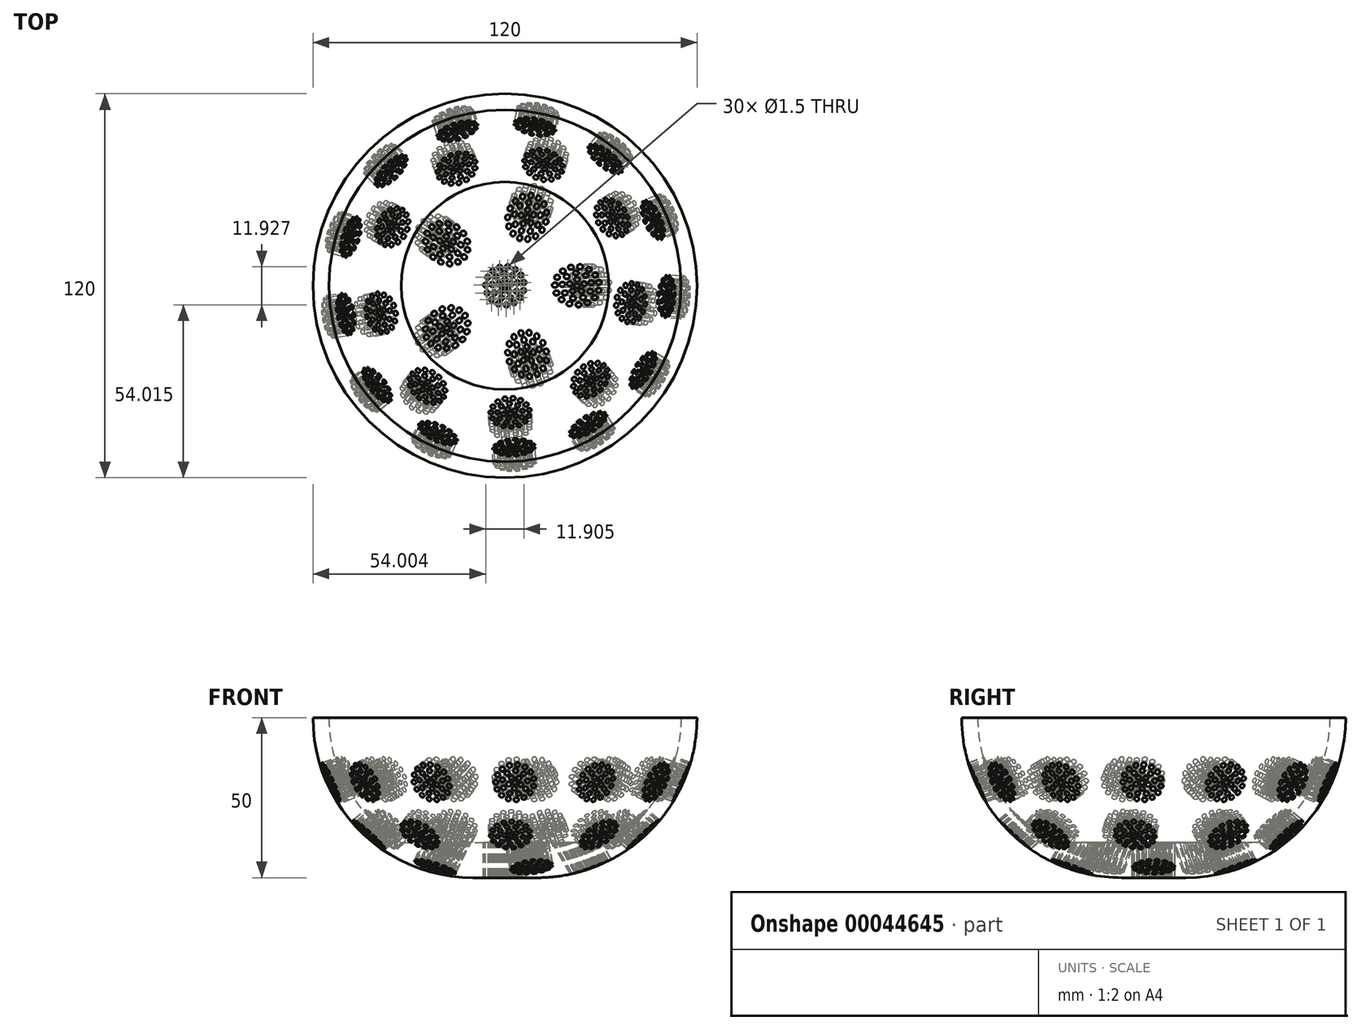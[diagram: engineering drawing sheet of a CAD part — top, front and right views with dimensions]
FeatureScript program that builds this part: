
annotation { "Feature Type Name" : "Feature", "Feature Type Description" : "" }
export const myFeature = defineFeature(function(context is Context, id is Id, definition is map)
    precondition{}
    {
        {
            var Q0;
            Q0=qCreatedBy(makeId("Front.planeOp"),FACE);
            var sketch = newSketch(context, id + "F0", { "sketchPlane" : qUnion([Q0])});
            skLineSegment(sketch, "E0", {"start": v(0, 0) * mm, "end": v(10, 0) * mm});
            skArc(sketch, "E1", {"start": v(10, 0) * mm, "mid": v(45.36, 14.64) * mm, "end": v(60, 50) * mm});
            skLineSegment(sketch, "E2", {"start": v(0, 0) * mm, "end": v(0, 50) * mm});
            skLineSegment(sketch, "E3", {"start": v(0, 50) * mm, "end": v(60, 50) * mm});
            skArc(sketch, "E4.0", {"start": v(32.45, 11) * mm, "mid": v(48.96, 27.47) * mm, "end": v(55, 50) * mm});
            skLineSegment(sketch, "E4.1", {"start": v(0, 11) * mm, "end": v(32.45, 11) * mm});
            skSolve(sketch);
        }
        {
            var Q0;
            {var subQ2=sQuery(id+"F0.wireOp",EDGE,"E0");Q0=makeQuery(id+"F0.imprint","IMPRINT",FACE,{"disambiguationData":[TD([[makeQuery(id+"F0.imprint","IMPRINT",EDGE,{"derivedFrom":subQ2}),1.0]])]});}
            var Q1;
            Q1=sQuery(id+"F0.wireOp",EDGE,"E2");
            revolve(context, id + "F1", {"entities" : qUnion([Q0]), "axis" : qUnion([Q1]), "revolveType" : RevolveType.FULL});
        }
        {
            var Q0;
            Q0=makeQuery(id+"F1.opRevolve","SWEPT_FACE",FACE,{"disambiguationData":[OSD([sQuery(id+"F0.wireOp",EDGE,"E4.1")])]});
            var sketch = newSketch(context, id + "F2", { "sketchPlane" : qUnion([Q0])});
            skCircle(sketch, "E5", {"center": v(0, 0) * mm, "radius": 0.75 * mm});
            skCircle(sketch, "E6", {"center": v(0, 2) * mm, "radius": 0.75 * mm});
            skCircle(sketch, "E7.1.0", {"center": v(-1.9, 0.62) * mm, "radius": 0.75 * mm});
            skCircle(sketch, "E7.2.0", {"center": v(-1.18, -1.62) * mm, "radius": 0.75 * mm});
            skCircle(sketch, "E7.3.0", {"center": v(1.18, -1.62) * mm, "radius": 0.75 * mm});
            skCircle(sketch, "E7.4.0", {"center": v(1.9, 0.62) * mm, "radius": 0.75 * mm});
            skLineSegment(sketch, "E8", {"start": v(0, 2) * mm, "end": v(1.9, 0.62) * mm, "construction": true});
            skLineSegment(sketch, "E9", {"start": v(0, 0) * mm, "end": v(0.95, 1.3) * mm, "construction": true});
            skLineSegment(sketch, "E10", {"start": v(0.95, 1.3) * mm, "end": v(2.35, 3.24) * mm, "construction": true});
            skCircle(sketch, "E11", {"center": v(2.35, 3.24) * mm, "radius": 0.75 * mm});
            skCircle(sketch, "E12.1.0", {"center": v(-0.28, 4) * mm, "radius": 0.75 * mm});
            skCircle(sketch, "E12.2.0", {"center": v(-2.78, 2.88) * mm, "radius": 0.75 * mm});
            skCircle(sketch, "E12.3.0", {"center": v(-3.98, 0.42) * mm, "radius": 0.75 * mm});
            skCircle(sketch, "E12.4.0", {"center": v(-3.32, -2.24) * mm, "radius": 0.75 * mm});
            skCircle(sketch, "E12.5.0", {"center": v(-1.1, -3.85) * mm, "radius": 0.75 * mm});
            skCircle(sketch, "E12.6.0", {"center": v(1.63, -3.65) * mm, "radius": 0.75 * mm});
            skCircle(sketch, "E13.1.7.0", {"center": v(3.6, -1.75) * mm, "radius": 0.75 * mm});
            skCircle(sketch, "E13.1.8.0", {"center": v(3.88, 0.97) * mm, "radius": 0.75 * mm});
            skLineSegment(sketch, "E14", {"start": v(3.88, 0.97) * mm, "end": v(2.35, 3.24) * mm, "construction": true});
            skLineSegment(sketch, "E15", {"start": v(0, 0) * mm, "end": v(3.12, 2.1) * mm, "construction": true});
            skLineSegment(sketch, "E16", {"start": v(3.12, 2.1) * mm, "end": v(4.97, 3.36) * mm, "construction": true});
            skCircle(sketch, "E17", {"center": v(4.97, 3.36) * mm, "radius": 0.75 * mm});
            skCircle(sketch, "E18.1.0", {"center": v(3.18, 5.09) * mm, "radius": 0.75 * mm});
            skCircle(sketch, "E18.2.0", {"center": v(0.84, 5.94) * mm, "radius": 0.75 * mm});
            skCircle(sketch, "E18.3.0", {"center": v(-1.65, 5.77) * mm, "radius": 0.75 * mm});
            skCircle(sketch, "E18.4.0", {"center": v(-3.86, 4.6) * mm, "radius": 0.75 * mm});
            skCircle(sketch, "E18.5.0", {"center": v(-5.4, 2.63) * mm, "radius": 0.75 * mm});
            skCircle(sketch, "E18.6.0", {"center": v(-6, 0.2) * mm, "radius": 0.75 * mm});
            skCircle(sketch, "E18.7.0", {"center": v(-5.56, -2.25) * mm, "radius": 0.75 * mm});
            skCircle(sketch, "E18.8.0", {"center": v(-4.17, -4.32) * mm, "radius": 0.75 * mm});
            skCircle(sketch, "E18.9.0", {"center": v(-2.05, -5.64) * mm, "radius": 0.75 * mm});
            skCircle(sketch, "E18.10.0", {"center": v(0.42, -5.99) * mm, "radius": 0.75 * mm});
            skCircle(sketch, "E18.11.0", {"center": v(2.82, -5.3) * mm, "radius": 0.75 * mm});
            skCircle(sketch, "E18.12.0", {"center": v(4.73, -3.7) * mm, "radius": 0.75 * mm});
            skCircle(sketch, "E18.13.0", {"center": v(5.82, -1.45) * mm, "radius": 0.75 * mm});
            skCircle(sketch, "E18.14.0", {"center": v(5.9, 1.04) * mm, "radius": 0.75 * mm});
            skSolve(sketch);
        }
        {
            var Q0;
            Q0=qSketchRegion(id+"F2",true);
            extrude(context, id + "F3", {"entities" : qUnion([Q0]), "operationType" : NewBodyOperationType.REMOVE, "oppositeDirection" : true, "depth" : 25 * mm});
        }
        {
            var Q0;
            Q0=makeQuery(id+"F1.opRevolve","SWEPT_FACE",FACE,{"disambiguationData":[OSD([sQuery(id+"F0.wireOp",EDGE,"E3")])]});
            var sketch = newSketch(context, id + "F4", { "sketchPlane" : qUnion([Q0])});
            skLineSegment(sketch, "E19", {"start": v(0, 55) * mm, "end": v(0, -55) * mm});
            skLineSegment(sketch, "E20", {"start": v(0, 0) * mm, "end": v(-29.42, 46.47) * mm});
            skLineSegment(sketch, "E21", {"start": v(0, 0) * mm, "end": v(-43.14, 34.11) * mm});
            skSolve(sketch);
        }
        {
            var Q0;
            Q0=makeQuery(id+"F3.boolean.opBoolean","COPY",FACE,{"derivedFrom":makeQuery(id+"F3.opExtrude","SWEPT_FACE",FACE,{"disambiguationData":[OSD([sQuery(id+"F2.wireOp",EDGE,"E18.7.0")])]})});
            var Q1;
            Q1=makeQuery(id+"F3.boolean.opBoolean","COPY",FACE,{"derivedFrom":makeQuery(id+"F3.opExtrude","SWEPT_FACE",FACE,{"disambiguationData":[OSD([sQuery(id+"F2.wireOp",EDGE,"E18.6.0")])]})});
            var Q2;
            Q2=makeQuery(id+"F3.boolean.opBoolean","COPY",FACE,{"derivedFrom":makeQuery(id+"F3.opExtrude","SWEPT_FACE",FACE,{"disambiguationData":[OSD([sQuery(id+"F2.wireOp",EDGE,"E18.5.0")])]})});
            var Q3;
            Q3=makeQuery(id+"F3.boolean.opBoolean","COPY",FACE,{"derivedFrom":makeQuery(id+"F3.opExtrude","SWEPT_FACE",FACE,{"disambiguationData":[OSD([sQuery(id+"F2.wireOp",EDGE,"E18.4.0")])]})});
            var Q4;
            Q4=makeQuery(id+"F3.boolean.opBoolean","COPY",FACE,{"derivedFrom":makeQuery(id+"F3.opExtrude","SWEPT_FACE",FACE,{"disambiguationData":[OSD([sQuery(id+"F2.wireOp",EDGE,"E18.3.0")])]})});
            var Q5;
            Q5=makeQuery(id+"F3.boolean.opBoolean","COPY",FACE,{"derivedFrom":makeQuery(id+"F3.opExtrude","SWEPT_FACE",FACE,{"disambiguationData":[OSD([sQuery(id+"F2.wireOp",EDGE,"E18.2.0")])]})});
            var Q6;
            Q6=makeQuery(id+"F3.boolean.opBoolean","COPY",FACE,{"derivedFrom":makeQuery(id+"F3.opExtrude","SWEPT_FACE",FACE,{"disambiguationData":[OSD([sQuery(id+"F2.wireOp",EDGE,"E18.1.0")])]})});
            var Q7;
            Q7=makeQuery(id+"F3.boolean.opBoolean","COPY",FACE,{"derivedFrom":makeQuery(id+"F3.opExtrude","SWEPT_FACE",FACE,{"disambiguationData":[OSD([sQuery(id+"F2.wireOp",EDGE,"E17")])]})});
            var Q8;
            Q8=makeQuery(id+"F3.boolean.opBoolean","COPY",FACE,{"derivedFrom":makeQuery(id+"F3.opExtrude","SWEPT_FACE",FACE,{"disambiguationData":[OSD([sQuery(id+"F2.wireOp",EDGE,"E18.14.0")])]})});
            var Q9;
            Q9=makeQuery(id+"F3.boolean.opBoolean","COPY",FACE,{"derivedFrom":makeQuery(id+"F3.opExtrude","SWEPT_FACE",FACE,{"disambiguationData":[OSD([sQuery(id+"F2.wireOp",EDGE,"E18.13.0")])]})});
            var Q10;
            Q10=makeQuery(id+"F3.boolean.opBoolean","COPY",FACE,{"derivedFrom":makeQuery(id+"F3.opExtrude","SWEPT_FACE",FACE,{"disambiguationData":[OSD([sQuery(id+"F2.wireOp",EDGE,"E18.12.0")])]})});
            var Q11;
            Q11=makeQuery(id+"F3.boolean.opBoolean","COPY",FACE,{"derivedFrom":makeQuery(id+"F3.opExtrude","SWEPT_FACE",FACE,{"disambiguationData":[OSD([sQuery(id+"F2.wireOp",EDGE,"E18.11.0")])]})});
            var Q12;
            Q12=makeQuery(id+"F3.boolean.opBoolean","COPY",FACE,{"derivedFrom":makeQuery(id+"F3.opExtrude","SWEPT_FACE",FACE,{"disambiguationData":[OSD([sQuery(id+"F2.wireOp",EDGE,"E18.10.0")])]})});
            var Q13;
            Q13=makeQuery(id+"F3.boolean.opBoolean","COPY",FACE,{"derivedFrom":makeQuery(id+"F3.opExtrude","SWEPT_FACE",FACE,{"disambiguationData":[OSD([sQuery(id+"F2.wireOp",EDGE,"E18.9.0")])]})});
            var Q14;
            Q14=makeQuery(id+"F3.boolean.opBoolean","COPY",FACE,{"derivedFrom":makeQuery(id+"F3.opExtrude","SWEPT_FACE",FACE,{"disambiguationData":[OSD([sQuery(id+"F2.wireOp",EDGE,"E18.8.0")])]})});
            var Q15;
            Q15=makeQuery(id+"F3.boolean.opBoolean","COPY",FACE,{"derivedFrom":makeQuery(id+"F3.opExtrude","SWEPT_FACE",FACE,{"disambiguationData":[OSD([sQuery(id+"F2.wireOp",EDGE,"E12.4.0")])]})});
            var Q16;
            Q16=makeQuery(id+"F3.boolean.opBoolean","COPY",FACE,{"derivedFrom":makeQuery(id+"F3.opExtrude","SWEPT_FACE",FACE,{"disambiguationData":[OSD([sQuery(id+"F2.wireOp",EDGE,"E12.3.0")])]})});
            var Q17;
            Q17=makeQuery(id+"F3.boolean.opBoolean","COPY",FACE,{"derivedFrom":makeQuery(id+"F3.opExtrude","SWEPT_FACE",FACE,{"disambiguationData":[OSD([sQuery(id+"F2.wireOp",EDGE,"E12.2.0")])]})});
            var Q18;
            Q18=makeQuery(id+"F3.boolean.opBoolean","COPY",FACE,{"derivedFrom":makeQuery(id+"F3.opExtrude","SWEPT_FACE",FACE,{"disambiguationData":[OSD([sQuery(id+"F2.wireOp",EDGE,"E12.1.0")])]})});
            var Q19;
            Q19=makeQuery(id+"F3.boolean.opBoolean","COPY",FACE,{"derivedFrom":makeQuery(id+"F3.opExtrude","SWEPT_FACE",FACE,{"disambiguationData":[OSD([sQuery(id+"F2.wireOp",EDGE,"E11")])]})});
            var Q20;
            Q20=makeQuery(id+"F3.boolean.opBoolean","COPY",FACE,{"derivedFrom":makeQuery(id+"F3.opExtrude","SWEPT_FACE",FACE,{"disambiguationData":[OSD([sQuery(id+"F2.wireOp",EDGE,"E13.1.8.0")])]})});
            var Q21;
            Q21=makeQuery(id+"F3.boolean.opBoolean","COPY",FACE,{"derivedFrom":makeQuery(id+"F3.opExtrude","SWEPT_FACE",FACE,{"disambiguationData":[OSD([sQuery(id+"F2.wireOp",EDGE,"E13.1.7.0")])]})});
            var Q22;
            Q22=makeQuery(id+"F3.boolean.opBoolean","COPY",FACE,{"derivedFrom":makeQuery(id+"F3.opExtrude","SWEPT_FACE",FACE,{"disambiguationData":[OSD([sQuery(id+"F2.wireOp",EDGE,"E12.6.0")])]})});
            var Q23;
            Q23=makeQuery(id+"F3.boolean.opBoolean","COPY",FACE,{"derivedFrom":makeQuery(id+"F3.opExtrude","SWEPT_FACE",FACE,{"disambiguationData":[OSD([sQuery(id+"F2.wireOp",EDGE,"E12.5.0")])]})});
            var Q24;
            Q24=makeQuery(id+"F3.boolean.opBoolean","COPY",FACE,{"derivedFrom":makeQuery(id+"F3.opExtrude","SWEPT_FACE",FACE,{"disambiguationData":[OSD([sQuery(id+"F2.wireOp",EDGE,"E7.2.0")])]})});
            var Q25;
            Q25=makeQuery(id+"F3.boolean.opBoolean","COPY",FACE,{"derivedFrom":makeQuery(id+"F3.opExtrude","SWEPT_FACE",FACE,{"disambiguationData":[OSD([sQuery(id+"F2.wireOp",EDGE,"E7.1.0")])]})});
            var Q26;
            Q26=makeQuery(id+"F3.boolean.opBoolean","COPY",FACE,{"derivedFrom":makeQuery(id+"F3.opExtrude","SWEPT_FACE",FACE,{"disambiguationData":[OSD([sQuery(id+"F2.wireOp",EDGE,"E6")])]})});
            var Q27;
            Q27=makeQuery(id+"F3.boolean.opBoolean","COPY",FACE,{"derivedFrom":makeQuery(id+"F3.opExtrude","SWEPT_FACE",FACE,{"disambiguationData":[OSD([sQuery(id+"F2.wireOp",EDGE,"E7.4.0")])]})});
            var Q28;
            Q28=makeQuery(id+"F3.boolean.opBoolean","COPY",FACE,{"derivedFrom":makeQuery(id+"F3.opExtrude","SWEPT_FACE",FACE,{"disambiguationData":[OSD([sQuery(id+"F2.wireOp",EDGE,"E7.3.0")])]})});
            var Q29;
            Q29=makeQuery(id+"F3.boolean.opBoolean","COPY",FACE,{"derivedFrom":makeQuery(id+"F3.opExtrude","SWEPT_FACE",FACE,{"disambiguationData":[OSD([sQuery(id+"F2.wireOp",EDGE,"E5")])]})});
            var Q30;
            Q30=sQuery(id+"F4.wireOp",EDGE,"E19");
            circularPattern(context, id + "F5", {"faces" : qUnion([Q0, Q1, Q2, Q3, Q4, Q5, Q6, Q7, Q8, Q9, Q10, Q11, Q12, Q13, Q14, Q15, Q16, Q17, Q18, Q19, Q20, Q21, Q22, Q23, Q24, Q25, Q26, Q27, Q28, Q29]), "axis" : qUnion([Q30]), "angle" : 30 * degree, "instanceCount" : 2, "patternType" : PatternType.FACE});
        }
        {
            var Q0;
            Q0=makeQuery(id+"F5.opPattern","COPY",FACE,{"derivedFrom":makeQuery(id+"F3.boolean.opBoolean","COPY",FACE,{"derivedFrom":makeQuery(id+"F3.opExtrude","SWEPT_FACE",FACE,{"disambiguationData":[OSD([sQuery(id+"F2.wireOp",EDGE,"E18.5.0")])]})}),"instanceName":"1"});
            var Q1;
            Q1=makeQuery(id+"F5.opPattern","COPY",FACE,{"derivedFrom":makeQuery(id+"F3.boolean.opBoolean","COPY",FACE,{"derivedFrom":makeQuery(id+"F3.opExtrude","SWEPT_FACE",FACE,{"disambiguationData":[OSD([sQuery(id+"F2.wireOp",EDGE,"E18.6.0")])]})}),"instanceName":"1"});
            var Q2;
            Q2=makeQuery(id+"F5.opPattern","COPY",FACE,{"derivedFrom":makeQuery(id+"F3.boolean.opBoolean","COPY",FACE,{"derivedFrom":makeQuery(id+"F3.opExtrude","SWEPT_FACE",FACE,{"disambiguationData":[OSD([sQuery(id+"F2.wireOp",EDGE,"E18.7.0")])]})}),"instanceName":"1"});
            var Q3;
            Q3=makeQuery(id+"F5.opPattern","COPY",FACE,{"derivedFrom":makeQuery(id+"F3.boolean.opBoolean","COPY",FACE,{"derivedFrom":makeQuery(id+"F3.opExtrude","SWEPT_FACE",FACE,{"disambiguationData":[OSD([sQuery(id+"F2.wireOp",EDGE,"E18.8.0")])]})}),"instanceName":"1"});
            var Q4;
            Q4=makeQuery(id+"F5.opPattern","COPY",FACE,{"derivedFrom":makeQuery(id+"F3.boolean.opBoolean","COPY",FACE,{"derivedFrom":makeQuery(id+"F3.opExtrude","SWEPT_FACE",FACE,{"disambiguationData":[OSD([sQuery(id+"F2.wireOp",EDGE,"E18.9.0")])]})}),"instanceName":"1"});
            var Q5;
            Q5=makeQuery(id+"F5.opPattern","COPY",FACE,{"derivedFrom":makeQuery(id+"F3.boolean.opBoolean","COPY",FACE,{"derivedFrom":makeQuery(id+"F3.opExtrude","SWEPT_FACE",FACE,{"disambiguationData":[OSD([sQuery(id+"F2.wireOp",EDGE,"E18.11.0")])]})}),"instanceName":"1"});
            var Q6;
            Q6=makeQuery(id+"F5.opPattern","COPY",FACE,{"derivedFrom":makeQuery(id+"F3.boolean.opBoolean","COPY",FACE,{"derivedFrom":makeQuery(id+"F3.opExtrude","SWEPT_FACE",FACE,{"disambiguationData":[OSD([sQuery(id+"F2.wireOp",EDGE,"E18.12.0")])]})}),"instanceName":"1"});
            var Q7;
            Q7=makeQuery(id+"F5.opPattern","COPY",FACE,{"derivedFrom":makeQuery(id+"F3.boolean.opBoolean","COPY",FACE,{"derivedFrom":makeQuery(id+"F3.opExtrude","SWEPT_FACE",FACE,{"disambiguationData":[OSD([sQuery(id+"F2.wireOp",EDGE,"E18.13.0")])]})}),"instanceName":"1"});
            var Q8;
            Q8=makeQuery(id+"F5.opPattern","COPY",FACE,{"derivedFrom":makeQuery(id+"F3.boolean.opBoolean","COPY",FACE,{"derivedFrom":makeQuery(id+"F3.opExtrude","SWEPT_FACE",FACE,{"disambiguationData":[OSD([sQuery(id+"F2.wireOp",EDGE,"E18.14.0")])]})}),"instanceName":"1"});
            var Q9;
            Q9=makeQuery(id+"F5.opPattern","COPY",FACE,{"derivedFrom":makeQuery(id+"F3.boolean.opBoolean","COPY",FACE,{"derivedFrom":makeQuery(id+"F3.opExtrude","SWEPT_FACE",FACE,{"disambiguationData":[OSD([sQuery(id+"F2.wireOp",EDGE,"E17")])]})}),"instanceName":"1"});
            var Q10;
            Q10=makeQuery(id+"F5.opPattern","COPY",FACE,{"derivedFrom":makeQuery(id+"F3.boolean.opBoolean","COPY",FACE,{"derivedFrom":makeQuery(id+"F3.opExtrude","SWEPT_FACE",FACE,{"disambiguationData":[OSD([sQuery(id+"F2.wireOp",EDGE,"E18.1.0")])]})}),"instanceName":"1"});
            var Q11;
            Q11=makeQuery(id+"F5.opPattern","COPY",FACE,{"derivedFrom":makeQuery(id+"F3.boolean.opBoolean","COPY",FACE,{"derivedFrom":makeQuery(id+"F3.opExtrude","SWEPT_FACE",FACE,{"disambiguationData":[OSD([sQuery(id+"F2.wireOp",EDGE,"E18.2.0")])]})}),"instanceName":"1"});
            var Q12;
            Q12=makeQuery(id+"F5.opPattern","COPY",FACE,{"derivedFrom":makeQuery(id+"F3.boolean.opBoolean","COPY",FACE,{"derivedFrom":makeQuery(id+"F3.opExtrude","SWEPT_FACE",FACE,{"disambiguationData":[OSD([sQuery(id+"F2.wireOp",EDGE,"E18.3.0")])]})}),"instanceName":"1"});
            var Q13;
            Q13=makeQuery(id+"F5.opPattern","COPY",FACE,{"derivedFrom":makeQuery(id+"F3.boolean.opBoolean","COPY",FACE,{"derivedFrom":makeQuery(id+"F3.opExtrude","SWEPT_FACE",FACE,{"disambiguationData":[OSD([sQuery(id+"F2.wireOp",EDGE,"E18.4.0")])]})}),"instanceName":"1"});
            var Q14;
            Q14=makeQuery(id+"F5.opPattern","COPY",FACE,{"derivedFrom":makeQuery(id+"F3.boolean.opBoolean","COPY",FACE,{"derivedFrom":makeQuery(id+"F3.opExtrude","SWEPT_FACE",FACE,{"disambiguationData":[OSD([sQuery(id+"F2.wireOp",EDGE,"E12.2.0")])]})}),"instanceName":"1"});
            var Q15;
            Q15=makeQuery(id+"F5.opPattern","COPY",FACE,{"derivedFrom":makeQuery(id+"F3.boolean.opBoolean","COPY",FACE,{"derivedFrom":makeQuery(id+"F3.opExtrude","SWEPT_FACE",FACE,{"disambiguationData":[OSD([sQuery(id+"F2.wireOp",EDGE,"E12.3.0")])]})}),"instanceName":"1"});
            var Q16;
            Q16=makeQuery(id+"F5.opPattern","COPY",FACE,{"derivedFrom":makeQuery(id+"F3.boolean.opBoolean","COPY",FACE,{"derivedFrom":makeQuery(id+"F3.opExtrude","SWEPT_FACE",FACE,{"disambiguationData":[OSD([sQuery(id+"F2.wireOp",EDGE,"E12.4.0")])]})}),"instanceName":"1"});
            var Q17;
            Q17=makeQuery(id+"F5.opPattern","COPY",FACE,{"derivedFrom":makeQuery(id+"F3.boolean.opBoolean","COPY",FACE,{"derivedFrom":makeQuery(id+"F3.opExtrude","SWEPT_FACE",FACE,{"disambiguationData":[OSD([sQuery(id+"F2.wireOp",EDGE,"E12.6.0")])]})}),"instanceName":"1"});
            var Q18;
            Q18=makeQuery(id+"F5.opPattern","COPY",FACE,{"derivedFrom":makeQuery(id+"F3.boolean.opBoolean","COPY",FACE,{"derivedFrom":makeQuery(id+"F3.opExtrude","SWEPT_FACE",FACE,{"disambiguationData":[OSD([sQuery(id+"F2.wireOp",EDGE,"E13.1.7.0")])]})}),"instanceName":"1"});
            var Q19;
            Q19=makeQuery(id+"F5.opPattern","COPY",FACE,{"derivedFrom":makeQuery(id+"F3.boolean.opBoolean","COPY",FACE,{"derivedFrom":makeQuery(id+"F3.opExtrude","SWEPT_FACE",FACE,{"disambiguationData":[OSD([sQuery(id+"F2.wireOp",EDGE,"E18.10.0")])]})}),"instanceName":"1"});
            var Q20;
            Q20=makeQuery(id+"F5.opPattern","COPY",FACE,{"derivedFrom":makeQuery(id+"F3.boolean.opBoolean","COPY",FACE,{"derivedFrom":makeQuery(id+"F3.opExtrude","SWEPT_FACE",FACE,{"disambiguationData":[OSD([sQuery(id+"F2.wireOp",EDGE,"E12.5.0")])]})}),"instanceName":"1"});
            var Q21;
            Q21=makeQuery(id+"F5.opPattern","COPY",FACE,{"derivedFrom":makeQuery(id+"F3.boolean.opBoolean","COPY",FACE,{"derivedFrom":makeQuery(id+"F3.opExtrude","SWEPT_FACE",FACE,{"disambiguationData":[OSD([sQuery(id+"F2.wireOp",EDGE,"E7.2.0")])]})}),"instanceName":"1"});
            var Q22;
            Q22=makeQuery(id+"F5.opPattern","COPY",FACE,{"derivedFrom":makeQuery(id+"F3.boolean.opBoolean","COPY",FACE,{"derivedFrom":makeQuery(id+"F3.opExtrude","SWEPT_FACE",FACE,{"disambiguationData":[OSD([sQuery(id+"F2.wireOp",EDGE,"E5")])]})}),"instanceName":"1"});
            var Q23;
            Q23=makeQuery(id+"F5.opPattern","COPY",FACE,{"derivedFrom":makeQuery(id+"F3.boolean.opBoolean","COPY",FACE,{"derivedFrom":makeQuery(id+"F3.opExtrude","SWEPT_FACE",FACE,{"disambiguationData":[OSD([sQuery(id+"F2.wireOp",EDGE,"E6")])]})}),"instanceName":"1"});
            var Q24;
            Q24=makeQuery(id+"F5.opPattern","COPY",FACE,{"derivedFrom":makeQuery(id+"F3.boolean.opBoolean","COPY",FACE,{"derivedFrom":makeQuery(id+"F3.opExtrude","SWEPT_FACE",FACE,{"disambiguationData":[OSD([sQuery(id+"F2.wireOp",EDGE,"E7.4.0")])]})}),"instanceName":"1"});
            var Q25;
            Q25=makeQuery(id+"F5.opPattern","COPY",FACE,{"derivedFrom":makeQuery(id+"F3.boolean.opBoolean","COPY",FACE,{"derivedFrom":makeQuery(id+"F3.opExtrude","SWEPT_FACE",FACE,{"disambiguationData":[OSD([sQuery(id+"F2.wireOp",EDGE,"E7.3.0")])]})}),"instanceName":"1"});
            var Q26;
            Q26=makeQuery(id+"F5.opPattern","COPY",FACE,{"derivedFrom":makeQuery(id+"F3.boolean.opBoolean","COPY",FACE,{"derivedFrom":makeQuery(id+"F3.opExtrude","SWEPT_FACE",FACE,{"disambiguationData":[OSD([sQuery(id+"F2.wireOp",EDGE,"E13.1.8.0")])]})}),"instanceName":"1"});
            var Q27;
            Q27=makeQuery(id+"F5.opPattern","COPY",FACE,{"derivedFrom":makeQuery(id+"F3.boolean.opBoolean","COPY",FACE,{"derivedFrom":makeQuery(id+"F3.opExtrude","SWEPT_FACE",FACE,{"disambiguationData":[OSD([sQuery(id+"F2.wireOp",EDGE,"E11")])]})}),"instanceName":"1"});
            var Q28;
            Q28=makeQuery(id+"F5.opPattern","COPY",FACE,{"derivedFrom":makeQuery(id+"F3.boolean.opBoolean","COPY",FACE,{"derivedFrom":makeQuery(id+"F3.opExtrude","SWEPT_FACE",FACE,{"disambiguationData":[OSD([sQuery(id+"F2.wireOp",EDGE,"E12.1.0")])]})}),"instanceName":"1"});
            var Q29;
            Q29=makeQuery(id+"F5.opPattern","COPY",FACE,{"derivedFrom":makeQuery(id+"F3.boolean.opBoolean","COPY",FACE,{"derivedFrom":makeQuery(id+"F3.opExtrude","SWEPT_FACE",FACE,{"disambiguationData":[OSD([sQuery(id+"F2.wireOp",EDGE,"E7.1.0")])]})}),"instanceName":"1"});
            var Q30;
            Q30=sQuery(id+"F0.wireOp",EDGE,"E2");
            circularPattern(context, id + "F6", {"faces" : qUnion([Q0, Q1, Q2, Q3, Q4, Q5, Q6, Q7, Q8, Q9, Q10, Q11, Q12, Q13, Q14, Q15, Q16, Q17, Q18, Q19, Q20, Q21, Q22, Q23, Q24, Q25, Q26, Q27, Q28, Q29]), "axis" : qUnion([Q30]), "angle" : 360 * degree, "instanceCount" : round(5), "equalSpace" : true, "patternType" : PatternType.FACE});
        }
        {
            var Q0;
            Q0=makeQuery(id+"F3.boolean.opBoolean","COPY",FACE,{"derivedFrom":makeQuery(id+"F3.opExtrude","SWEPT_FACE",FACE,{"disambiguationData":[OSD([sQuery(id+"F2.wireOp",EDGE,"E18.1.0")])]})});
            var Q1;
            Q1=makeQuery(id+"F3.boolean.opBoolean","COPY",FACE,{"derivedFrom":makeQuery(id+"F3.opExtrude","SWEPT_FACE",FACE,{"disambiguationData":[OSD([sQuery(id+"F2.wireOp",EDGE,"E18.2.0")])]})});
            var Q2;
            Q2=makeQuery(id+"F3.boolean.opBoolean","COPY",FACE,{"derivedFrom":makeQuery(id+"F3.opExtrude","SWEPT_FACE",FACE,{"disambiguationData":[OSD([sQuery(id+"F2.wireOp",EDGE,"E18.3.0")])]})});
            var Q3;
            Q3=makeQuery(id+"F3.boolean.opBoolean","COPY",FACE,{"derivedFrom":makeQuery(id+"F3.opExtrude","SWEPT_FACE",FACE,{"disambiguationData":[OSD([sQuery(id+"F2.wireOp",EDGE,"E18.4.0")])]})});
            var Q4;
            Q4=makeQuery(id+"F3.boolean.opBoolean","COPY",FACE,{"derivedFrom":makeQuery(id+"F3.opExtrude","SWEPT_FACE",FACE,{"disambiguationData":[OSD([sQuery(id+"F2.wireOp",EDGE,"E18.5.0")])]})});
            var Q5;
            Q5=makeQuery(id+"F3.boolean.opBoolean","COPY",FACE,{"derivedFrom":makeQuery(id+"F3.opExtrude","SWEPT_FACE",FACE,{"disambiguationData":[OSD([sQuery(id+"F2.wireOp",EDGE,"E18.6.0")])]})});
            var Q6;
            Q6=makeQuery(id+"F3.boolean.opBoolean","COPY",FACE,{"derivedFrom":makeQuery(id+"F3.opExtrude","SWEPT_FACE",FACE,{"disambiguationData":[OSD([sQuery(id+"F2.wireOp",EDGE,"E18.7.0")])]})});
            var Q7;
            Q7=makeQuery(id+"F3.boolean.opBoolean","COPY",FACE,{"derivedFrom":makeQuery(id+"F3.opExtrude","SWEPT_FACE",FACE,{"disambiguationData":[OSD([sQuery(id+"F2.wireOp",EDGE,"E18.8.0")])]})});
            var Q8;
            Q8=makeQuery(id+"F3.boolean.opBoolean","COPY",FACE,{"derivedFrom":makeQuery(id+"F3.opExtrude","SWEPT_FACE",FACE,{"disambiguationData":[OSD([sQuery(id+"F2.wireOp",EDGE,"E18.9.0")])]})});
            var Q9;
            Q9=makeQuery(id+"F3.boolean.opBoolean","COPY",FACE,{"derivedFrom":makeQuery(id+"F3.opExtrude","SWEPT_FACE",FACE,{"disambiguationData":[OSD([sQuery(id+"F2.wireOp",EDGE,"E18.10.0")])]})});
            var Q10;
            Q10=makeQuery(id+"F3.boolean.opBoolean","COPY",FACE,{"derivedFrom":makeQuery(id+"F3.opExtrude","SWEPT_FACE",FACE,{"disambiguationData":[OSD([sQuery(id+"F2.wireOp",EDGE,"E18.11.0")])]})});
            var Q11;
            Q11=makeQuery(id+"F3.boolean.opBoolean","COPY",FACE,{"derivedFrom":makeQuery(id+"F3.opExtrude","SWEPT_FACE",FACE,{"disambiguationData":[OSD([sQuery(id+"F2.wireOp",EDGE,"E18.12.0")])]})});
            var Q12;
            Q12=makeQuery(id+"F3.boolean.opBoolean","COPY",FACE,{"derivedFrom":makeQuery(id+"F3.opExtrude","SWEPT_FACE",FACE,{"disambiguationData":[OSD([sQuery(id+"F2.wireOp",EDGE,"E18.13.0")])]})});
            var Q13;
            Q13=makeQuery(id+"F3.boolean.opBoolean","COPY",FACE,{"derivedFrom":makeQuery(id+"F3.opExtrude","SWEPT_FACE",FACE,{"disambiguationData":[OSD([sQuery(id+"F2.wireOp",EDGE,"E18.14.0")])]})});
            var Q14;
            Q14=makeQuery(id+"F3.boolean.opBoolean","COPY",FACE,{"derivedFrom":makeQuery(id+"F3.opExtrude","SWEPT_FACE",FACE,{"disambiguationData":[OSD([sQuery(id+"F2.wireOp",EDGE,"E13.1.8.0")])]})});
            var Q15;
            Q15=makeQuery(id+"F3.boolean.opBoolean","COPY",FACE,{"derivedFrom":makeQuery(id+"F3.opExtrude","SWEPT_FACE",FACE,{"disambiguationData":[OSD([sQuery(id+"F2.wireOp",EDGE,"E11")])]})});
            var Q16;
            Q16=makeQuery(id+"F3.boolean.opBoolean","COPY",FACE,{"derivedFrom":makeQuery(id+"F3.opExtrude","SWEPT_FACE",FACE,{"disambiguationData":[OSD([sQuery(id+"F2.wireOp",EDGE,"E12.1.0")])]})});
            var Q17;
            Q17=makeQuery(id+"F3.boolean.opBoolean","COPY",FACE,{"derivedFrom":makeQuery(id+"F3.opExtrude","SWEPT_FACE",FACE,{"disambiguationData":[OSD([sQuery(id+"F2.wireOp",EDGE,"E12.2.0")])]})});
            var Q18;
            Q18=makeQuery(id+"F3.boolean.opBoolean","COPY",FACE,{"derivedFrom":makeQuery(id+"F3.opExtrude","SWEPT_FACE",FACE,{"disambiguationData":[OSD([sQuery(id+"F2.wireOp",EDGE,"E12.3.0")])]})});
            var Q19;
            Q19=makeQuery(id+"F3.boolean.opBoolean","COPY",FACE,{"derivedFrom":makeQuery(id+"F3.opExtrude","SWEPT_FACE",FACE,{"disambiguationData":[OSD([sQuery(id+"F2.wireOp",EDGE,"E12.4.0")])]})});
            var Q20;
            Q20=makeQuery(id+"F3.boolean.opBoolean","COPY",FACE,{"derivedFrom":makeQuery(id+"F3.opExtrude","SWEPT_FACE",FACE,{"disambiguationData":[OSD([sQuery(id+"F2.wireOp",EDGE,"E12.5.0")])]})});
            var Q21;
            Q21=makeQuery(id+"F3.boolean.opBoolean","COPY",FACE,{"derivedFrom":makeQuery(id+"F3.opExtrude","SWEPT_FACE",FACE,{"disambiguationData":[OSD([sQuery(id+"F2.wireOp",EDGE,"E12.6.0")])]})});
            var Q22;
            Q22=makeQuery(id+"F3.boolean.opBoolean","COPY",FACE,{"derivedFrom":makeQuery(id+"F3.opExtrude","SWEPT_FACE",FACE,{"disambiguationData":[OSD([sQuery(id+"F2.wireOp",EDGE,"E13.1.7.0")])]})});
            var Q23;
            Q23=makeQuery(id+"F3.boolean.opBoolean","COPY",FACE,{"derivedFrom":makeQuery(id+"F3.opExtrude","SWEPT_FACE",FACE,{"disambiguationData":[OSD([sQuery(id+"F2.wireOp",EDGE,"E7.4.0")])]})});
            var Q24;
            Q24=makeQuery(id+"F3.boolean.opBoolean","COPY",FACE,{"derivedFrom":makeQuery(id+"F3.opExtrude","SWEPT_FACE",FACE,{"disambiguationData":[OSD([sQuery(id+"F2.wireOp",EDGE,"E6")])]})});
            var Q25;
            Q25=makeQuery(id+"F3.boolean.opBoolean","COPY",FACE,{"derivedFrom":makeQuery(id+"F3.opExtrude","SWEPT_FACE",FACE,{"disambiguationData":[OSD([sQuery(id+"F2.wireOp",EDGE,"E7.1.0")])]})});
            var Q26;
            Q26=makeQuery(id+"F3.boolean.opBoolean","COPY",FACE,{"derivedFrom":makeQuery(id+"F3.opExtrude","SWEPT_FACE",FACE,{"disambiguationData":[OSD([sQuery(id+"F2.wireOp",EDGE,"E7.2.0")])]})});
            var Q27;
            Q27=makeQuery(id+"F3.boolean.opBoolean","COPY",FACE,{"derivedFrom":makeQuery(id+"F3.opExtrude","SWEPT_FACE",FACE,{"disambiguationData":[OSD([sQuery(id+"F2.wireOp",EDGE,"E5")])]})});
            var Q28;
            Q28=makeQuery(id+"F3.boolean.opBoolean","COPY",FACE,{"derivedFrom":makeQuery(id+"F3.opExtrude","SWEPT_FACE",FACE,{"disambiguationData":[OSD([sQuery(id+"F2.wireOp",EDGE,"E7.3.0")])]})});
            var Q29;
            Q29=makeQuery(id+"F3.boolean.opBoolean","COPY",FACE,{"derivedFrom":makeQuery(id+"F3.opExtrude","SWEPT_FACE",FACE,{"disambiguationData":[OSD([sQuery(id+"F2.wireOp",EDGE,"E17")])]})});
            var Q30;
            Q30=sQuery(id+"F4.wireOp",EDGE,"E20");
            circularPattern(context, id + "F7", {"faces" : qUnion([Q0, Q1, Q2, Q3, Q4, Q5, Q6, Q7, Q8, Q9, Q10, Q11, Q12, Q13, Q14, Q15, Q16, Q17, Q18, Q19, Q20, Q21, Q22, Q23, Q24, Q25, Q26, Q27, Q28, Q29]), "axis" : qUnion([Q30]), "angle" : 50 * degree, "instanceCount" : 2, "oppositeDirection" : true, "patternType" : PatternType.FACE});
        }
        {
            var Q0;
            Q0=makeQuery(id+"F7.opPattern","COPY",FACE,{"derivedFrom":makeQuery(id+"F3.boolean.opBoolean","COPY",FACE,{"derivedFrom":makeQuery(id+"F3.opExtrude","SWEPT_FACE",FACE,{"disambiguationData":[OSD([sQuery(id+"F2.wireOp",EDGE,"E18.10.0")])]})}),"instanceName":"1"});
            var Q1;
            Q1=makeQuery(id+"F7.opPattern","COPY",FACE,{"derivedFrom":makeQuery(id+"F3.boolean.opBoolean","COPY",FACE,{"derivedFrom":makeQuery(id+"F3.opExtrude","SWEPT_FACE",FACE,{"disambiguationData":[OSD([sQuery(id+"F2.wireOp",EDGE,"E18.9.0")])]})}),"instanceName":"1"});
            var Q2;
            Q2=makeQuery(id+"F7.opPattern","COPY",FACE,{"derivedFrom":makeQuery(id+"F3.boolean.opBoolean","COPY",FACE,{"derivedFrom":makeQuery(id+"F3.opExtrude","SWEPT_FACE",FACE,{"disambiguationData":[OSD([sQuery(id+"F2.wireOp",EDGE,"E18.8.0")])]})}),"instanceName":"1"});
            var Q3;
            Q3=makeQuery(id+"F7.opPattern","COPY",FACE,{"derivedFrom":makeQuery(id+"F3.boolean.opBoolean","COPY",FACE,{"derivedFrom":makeQuery(id+"F3.opExtrude","SWEPT_FACE",FACE,{"disambiguationData":[OSD([sQuery(id+"F2.wireOp",EDGE,"E18.7.0")])]})}),"instanceName":"1"});
            var Q4;
            Q4=makeQuery(id+"F7.opPattern","COPY",FACE,{"derivedFrom":makeQuery(id+"F3.boolean.opBoolean","COPY",FACE,{"derivedFrom":makeQuery(id+"F3.opExtrude","SWEPT_FACE",FACE,{"disambiguationData":[OSD([sQuery(id+"F2.wireOp",EDGE,"E18.6.0")])]})}),"instanceName":"1"});
            var Q5;
            Q5=makeQuery(id+"F7.opPattern","COPY",FACE,{"derivedFrom":makeQuery(id+"F3.boolean.opBoolean","COPY",FACE,{"derivedFrom":makeQuery(id+"F3.opExtrude","SWEPT_FACE",FACE,{"disambiguationData":[OSD([sQuery(id+"F2.wireOp",EDGE,"E18.5.0")])]})}),"instanceName":"1"});
            var Q6;
            Q6=makeQuery(id+"F7.opPattern","COPY",FACE,{"derivedFrom":makeQuery(id+"F3.boolean.opBoolean","COPY",FACE,{"derivedFrom":makeQuery(id+"F3.opExtrude","SWEPT_FACE",FACE,{"disambiguationData":[OSD([sQuery(id+"F2.wireOp",EDGE,"E18.4.0")])]})}),"instanceName":"1"});
            var Q7;
            Q7=makeQuery(id+"F7.opPattern","COPY",FACE,{"derivedFrom":makeQuery(id+"F3.boolean.opBoolean","COPY",FACE,{"derivedFrom":makeQuery(id+"F3.opExtrude","SWEPT_FACE",FACE,{"disambiguationData":[OSD([sQuery(id+"F2.wireOp",EDGE,"E18.3.0")])]})}),"instanceName":"1"});
            var Q8;
            Q8=makeQuery(id+"F7.opPattern","COPY",FACE,{"derivedFrom":makeQuery(id+"F3.boolean.opBoolean","COPY",FACE,{"derivedFrom":makeQuery(id+"F3.opExtrude","SWEPT_FACE",FACE,{"disambiguationData":[OSD([sQuery(id+"F2.wireOp",EDGE,"E12.2.0")])]})}),"instanceName":"1"});
            var Q9;
            Q9=makeQuery(id+"F7.opPattern","COPY",FACE,{"derivedFrom":makeQuery(id+"F3.boolean.opBoolean","COPY",FACE,{"derivedFrom":makeQuery(id+"F3.opExtrude","SWEPT_FACE",FACE,{"disambiguationData":[OSD([sQuery(id+"F2.wireOp",EDGE,"E12.3.0")])]})}),"instanceName":"1"});
            var Q10;
            Q10=makeQuery(id+"F7.opPattern","COPY",FACE,{"derivedFrom":makeQuery(id+"F3.boolean.opBoolean","COPY",FACE,{"derivedFrom":makeQuery(id+"F3.opExtrude","SWEPT_FACE",FACE,{"disambiguationData":[OSD([sQuery(id+"F2.wireOp",EDGE,"E12.4.0")])]})}),"instanceName":"1"});
            var Q11;
            Q11=makeQuery(id+"F7.opPattern","COPY",FACE,{"derivedFrom":makeQuery(id+"F3.boolean.opBoolean","COPY",FACE,{"derivedFrom":makeQuery(id+"F3.opExtrude","SWEPT_FACE",FACE,{"disambiguationData":[OSD([sQuery(id+"F2.wireOp",EDGE,"E12.5.0")])]})}),"instanceName":"1"});
            var Q12;
            Q12=makeQuery(id+"F7.opPattern","COPY",FACE,{"derivedFrom":makeQuery(id+"F3.boolean.opBoolean","COPY",FACE,{"derivedFrom":makeQuery(id+"F3.opExtrude","SWEPT_FACE",FACE,{"disambiguationData":[OSD([sQuery(id+"F2.wireOp",EDGE,"E12.6.0")])]})}),"instanceName":"1"});
            var Q13;
            Q13=makeQuery(id+"F7.opPattern","COPY",FACE,{"derivedFrom":makeQuery(id+"F3.boolean.opBoolean","COPY",FACE,{"derivedFrom":makeQuery(id+"F3.opExtrude","SWEPT_FACE",FACE,{"disambiguationData":[OSD([sQuery(id+"F2.wireOp",EDGE,"E7.2.0")])]})}),"instanceName":"1"});
            var Q14;
            Q14=makeQuery(id+"F7.opPattern","COPY",FACE,{"derivedFrom":makeQuery(id+"F3.boolean.opBoolean","COPY",FACE,{"derivedFrom":makeQuery(id+"F3.opExtrude","SWEPT_FACE",FACE,{"disambiguationData":[OSD([sQuery(id+"F2.wireOp",EDGE,"E7.1.0")])]})}),"instanceName":"1"});
            var Q15;
            Q15=makeQuery(id+"F7.opPattern","COPY",FACE,{"derivedFrom":makeQuery(id+"F3.boolean.opBoolean","COPY",FACE,{"derivedFrom":makeQuery(id+"F3.opExtrude","SWEPT_FACE",FACE,{"disambiguationData":[OSD([sQuery(id+"F2.wireOp",EDGE,"E6")])]})}),"instanceName":"1"});
            var Q16;
            Q16=makeQuery(id+"F7.opPattern","COPY",FACE,{"derivedFrom":makeQuery(id+"F3.boolean.opBoolean","COPY",FACE,{"derivedFrom":makeQuery(id+"F3.opExtrude","SWEPT_FACE",FACE,{"disambiguationData":[OSD([sQuery(id+"F2.wireOp",EDGE,"E12.1.0")])]})}),"instanceName":"1"});
            var Q17;
            Q17=makeQuery(id+"F7.opPattern","COPY",FACE,{"derivedFrom":makeQuery(id+"F3.boolean.opBoolean","COPY",FACE,{"derivedFrom":makeQuery(id+"F3.opExtrude","SWEPT_FACE",FACE,{"disambiguationData":[OSD([sQuery(id+"F2.wireOp",EDGE,"E18.2.0")])]})}),"instanceName":"1"});
            var Q18;
            Q18=makeQuery(id+"F7.opPattern","COPY",FACE,{"derivedFrom":makeQuery(id+"F3.boolean.opBoolean","COPY",FACE,{"derivedFrom":makeQuery(id+"F3.opExtrude","SWEPT_FACE",FACE,{"disambiguationData":[OSD([sQuery(id+"F2.wireOp",EDGE,"E18.1.0")])]})}),"instanceName":"1"});
            var Q19;
            Q19=makeQuery(id+"F7.opPattern","COPY",FACE,{"derivedFrom":makeQuery(id+"F3.boolean.opBoolean","COPY",FACE,{"derivedFrom":makeQuery(id+"F3.opExtrude","SWEPT_FACE",FACE,{"disambiguationData":[OSD([sQuery(id+"F2.wireOp",EDGE,"E11")])]})}),"instanceName":"1"});
            var Q20;
            Q20=makeQuery(id+"F7.opPattern","COPY",FACE,{"derivedFrom":makeQuery(id+"F3.boolean.opBoolean","COPY",FACE,{"derivedFrom":makeQuery(id+"F3.opExtrude","SWEPT_FACE",FACE,{"disambiguationData":[OSD([sQuery(id+"F2.wireOp",EDGE,"E7.4.0")])]})}),"instanceName":"1"});
            var Q21;
            Q21=makeQuery(id+"F7.opPattern","COPY",FACE,{"derivedFrom":makeQuery(id+"F3.boolean.opBoolean","COPY",FACE,{"derivedFrom":makeQuery(id+"F3.opExtrude","SWEPT_FACE",FACE,{"disambiguationData":[OSD([sQuery(id+"F2.wireOp",EDGE,"E5")])]})}),"instanceName":"1"});
            var Q22;
            Q22=makeQuery(id+"F7.opPattern","COPY",FACE,{"derivedFrom":makeQuery(id+"F3.boolean.opBoolean","COPY",FACE,{"derivedFrom":makeQuery(id+"F3.opExtrude","SWEPT_FACE",FACE,{"disambiguationData":[OSD([sQuery(id+"F2.wireOp",EDGE,"E7.3.0")])]})}),"instanceName":"1"});
            var Q23;
            Q23=makeQuery(id+"F7.opPattern","COPY",FACE,{"derivedFrom":makeQuery(id+"F3.boolean.opBoolean","COPY",FACE,{"derivedFrom":makeQuery(id+"F3.opExtrude","SWEPT_FACE",FACE,{"disambiguationData":[OSD([sQuery(id+"F2.wireOp",EDGE,"E18.11.0")])]})}),"instanceName":"1"});
            var Q24;
            Q24=makeQuery(id+"F7.opPattern","COPY",FACE,{"derivedFrom":makeQuery(id+"F3.boolean.opBoolean","COPY",FACE,{"derivedFrom":makeQuery(id+"F3.opExtrude","SWEPT_FACE",FACE,{"disambiguationData":[OSD([sQuery(id+"F2.wireOp",EDGE,"E18.12.0")])]})}),"instanceName":"1"});
            var Q25;
            Q25=makeQuery(id+"F7.opPattern","COPY",FACE,{"derivedFrom":makeQuery(id+"F3.boolean.opBoolean","COPY",FACE,{"derivedFrom":makeQuery(id+"F3.opExtrude","SWEPT_FACE",FACE,{"disambiguationData":[OSD([sQuery(id+"F2.wireOp",EDGE,"E13.1.7.0")])]})}),"instanceName":"1"});
            var Q26;
            Q26=makeQuery(id+"F7.opPattern","COPY",FACE,{"derivedFrom":makeQuery(id+"F3.boolean.opBoolean","COPY",FACE,{"derivedFrom":makeQuery(id+"F3.opExtrude","SWEPT_FACE",FACE,{"disambiguationData":[OSD([sQuery(id+"F2.wireOp",EDGE,"E18.13.0")])]})}),"instanceName":"1"});
            var Q27;
            Q27=makeQuery(id+"F7.opPattern","COPY",FACE,{"derivedFrom":makeQuery(id+"F3.boolean.opBoolean","COPY",FACE,{"derivedFrom":makeQuery(id+"F3.opExtrude","SWEPT_FACE",FACE,{"disambiguationData":[OSD([sQuery(id+"F2.wireOp",EDGE,"E18.14.0")])]})}),"instanceName":"1"});
            var Q28;
            Q28=makeQuery(id+"F7.opPattern","COPY",FACE,{"derivedFrom":makeQuery(id+"F3.boolean.opBoolean","COPY",FACE,{"derivedFrom":makeQuery(id+"F3.opExtrude","SWEPT_FACE",FACE,{"disambiguationData":[OSD([sQuery(id+"F2.wireOp",EDGE,"E13.1.8.0")])]})}),"instanceName":"1"});
            var Q29;
            Q29=makeQuery(id+"F7.opPattern","COPY",FACE,{"derivedFrom":makeQuery(id+"F3.boolean.opBoolean","COPY",FACE,{"derivedFrom":makeQuery(id+"F3.opExtrude","SWEPT_FACE",FACE,{"disambiguationData":[OSD([sQuery(id+"F2.wireOp",EDGE,"E17")])]})}),"instanceName":"1"});
            var Q30;
            Q30=sQuery(id+"F0.wireOp",EDGE,"E2");
            circularPattern(context, id + "F8", {"faces" : qUnion([Q0, Q1, Q2, Q3, Q4, Q5, Q6, Q7, Q8, Q9, Q10, Q11, Q12, Q13, Q14, Q15, Q16, Q17, Q18, Q19, Q20, Q21, Q22, Q23, Q24, Q25, Q26, Q27, Q28, Q29]), "axis" : qUnion([Q30]), "angle" : 360 * degree, "instanceCount" : round(9), "equalSpace" : true, "patternType" : PatternType.FACE});
        }
        {
            var Q0;
            Q0=makeQuery(id+"F3.boolean.opBoolean","COPY",FACE,{"derivedFrom":makeQuery(id+"F3.opExtrude","SWEPT_FACE",FACE,{"disambiguationData":[OSD([sQuery(id+"F2.wireOp",EDGE,"E18.14.0")])]})});
            var Q1;
            Q1=makeQuery(id+"F3.boolean.opBoolean","COPY",FACE,{"derivedFrom":makeQuery(id+"F3.opExtrude","SWEPT_FACE",FACE,{"disambiguationData":[OSD([sQuery(id+"F2.wireOp",EDGE,"E17")])]})});
            var Q2;
            Q2=makeQuery(id+"F3.boolean.opBoolean","COPY",FACE,{"derivedFrom":makeQuery(id+"F3.opExtrude","SWEPT_FACE",FACE,{"disambiguationData":[OSD([sQuery(id+"F2.wireOp",EDGE,"E18.1.0")])]})});
            var Q3;
            Q3=makeQuery(id+"F3.boolean.opBoolean","COPY",FACE,{"derivedFrom":makeQuery(id+"F3.opExtrude","SWEPT_FACE",FACE,{"disambiguationData":[OSD([sQuery(id+"F2.wireOp",EDGE,"E18.2.0")])]})});
            var Q4;
            Q4=makeQuery(id+"F3.boolean.opBoolean","COPY",FACE,{"derivedFrom":makeQuery(id+"F3.opExtrude","SWEPT_FACE",FACE,{"disambiguationData":[OSD([sQuery(id+"F2.wireOp",EDGE,"E18.3.0")])]})});
            var Q5;
            Q5=makeQuery(id+"F3.boolean.opBoolean","COPY",FACE,{"derivedFrom":makeQuery(id+"F3.opExtrude","SWEPT_FACE",FACE,{"disambiguationData":[OSD([sQuery(id+"F2.wireOp",EDGE,"E18.4.0")])]})});
            var Q6;
            Q6=makeQuery(id+"F3.boolean.opBoolean","COPY",FACE,{"derivedFrom":makeQuery(id+"F3.opExtrude","SWEPT_FACE",FACE,{"disambiguationData":[OSD([sQuery(id+"F2.wireOp",EDGE,"E18.5.0")])]})});
            var Q7;
            Q7=makeQuery(id+"F3.boolean.opBoolean","COPY",FACE,{"derivedFrom":makeQuery(id+"F3.opExtrude","SWEPT_FACE",FACE,{"disambiguationData":[OSD([sQuery(id+"F2.wireOp",EDGE,"E18.6.0")])]})});
            var Q8;
            Q8=makeQuery(id+"F3.boolean.opBoolean","COPY",FACE,{"derivedFrom":makeQuery(id+"F3.opExtrude","SWEPT_FACE",FACE,{"disambiguationData":[OSD([sQuery(id+"F2.wireOp",EDGE,"E18.7.0")])]})});
            var Q9;
            Q9=makeQuery(id+"F3.boolean.opBoolean","COPY",FACE,{"derivedFrom":makeQuery(id+"F3.opExtrude","SWEPT_FACE",FACE,{"disambiguationData":[OSD([sQuery(id+"F2.wireOp",EDGE,"E18.8.0")])]})});
            var Q10;
            Q10=makeQuery(id+"F3.boolean.opBoolean","COPY",FACE,{"derivedFrom":makeQuery(id+"F3.opExtrude","SWEPT_FACE",FACE,{"disambiguationData":[OSD([sQuery(id+"F2.wireOp",EDGE,"E18.9.0")])]})});
            var Q11;
            Q11=makeQuery(id+"F3.boolean.opBoolean","COPY",FACE,{"derivedFrom":makeQuery(id+"F3.opExtrude","SWEPT_FACE",FACE,{"disambiguationData":[OSD([sQuery(id+"F2.wireOp",EDGE,"E18.10.0")])]})});
            var Q12;
            Q12=makeQuery(id+"F3.boolean.opBoolean","COPY",FACE,{"derivedFrom":makeQuery(id+"F3.opExtrude","SWEPT_FACE",FACE,{"disambiguationData":[OSD([sQuery(id+"F2.wireOp",EDGE,"E18.11.0")])]})});
            var Q13;
            Q13=makeQuery(id+"F3.boolean.opBoolean","COPY",FACE,{"derivedFrom":makeQuery(id+"F3.opExtrude","SWEPT_FACE",FACE,{"disambiguationData":[OSD([sQuery(id+"F2.wireOp",EDGE,"E18.12.0")])]})});
            var Q14;
            Q14=makeQuery(id+"F3.boolean.opBoolean","COPY",FACE,{"derivedFrom":makeQuery(id+"F3.opExtrude","SWEPT_FACE",FACE,{"disambiguationData":[OSD([sQuery(id+"F2.wireOp",EDGE,"E18.13.0")])]})});
            var Q15;
            Q15=makeQuery(id+"F3.boolean.opBoolean","COPY",FACE,{"derivedFrom":makeQuery(id+"F3.opExtrude","SWEPT_FACE",FACE,{"disambiguationData":[OSD([sQuery(id+"F2.wireOp",EDGE,"E13.1.8.0")])]})});
            var Q16;
            Q16=makeQuery(id+"F3.boolean.opBoolean","COPY",FACE,{"derivedFrom":makeQuery(id+"F3.opExtrude","SWEPT_FACE",FACE,{"disambiguationData":[OSD([sQuery(id+"F2.wireOp",EDGE,"E11")])]})});
            var Q17;
            Q17=makeQuery(id+"F3.boolean.opBoolean","COPY",FACE,{"derivedFrom":makeQuery(id+"F3.opExtrude","SWEPT_FACE",FACE,{"disambiguationData":[OSD([sQuery(id+"F2.wireOp",EDGE,"E12.1.0")])]})});
            var Q18;
            Q18=makeQuery(id+"F3.boolean.opBoolean","COPY",FACE,{"derivedFrom":makeQuery(id+"F3.opExtrude","SWEPT_FACE",FACE,{"disambiguationData":[OSD([sQuery(id+"F2.wireOp",EDGE,"E6")])]})});
            var Q19;
            Q19=makeQuery(id+"F3.boolean.opBoolean","COPY",FACE,{"derivedFrom":makeQuery(id+"F3.opExtrude","SWEPT_FACE",FACE,{"disambiguationData":[OSD([sQuery(id+"F2.wireOp",EDGE,"E7.4.0")])]})});
            var Q20;
            Q20=makeQuery(id+"F3.boolean.opBoolean","COPY",FACE,{"derivedFrom":makeQuery(id+"F3.opExtrude","SWEPT_FACE",FACE,{"disambiguationData":[OSD([sQuery(id+"F2.wireOp",EDGE,"E13.1.7.0")])]})});
            var Q21;
            Q21=makeQuery(id+"F3.boolean.opBoolean","COPY",FACE,{"derivedFrom":makeQuery(id+"F3.opExtrude","SWEPT_FACE",FACE,{"disambiguationData":[OSD([sQuery(id+"F2.wireOp",EDGE,"E7.3.0")])]})});
            var Q22;
            Q22=makeQuery(id+"F3.boolean.opBoolean","COPY",FACE,{"derivedFrom":makeQuery(id+"F3.opExtrude","SWEPT_FACE",FACE,{"disambiguationData":[OSD([sQuery(id+"F2.wireOp",EDGE,"E5")])]})});
            var Q23;
            Q23=makeQuery(id+"F3.boolean.opBoolean","COPY",FACE,{"derivedFrom":makeQuery(id+"F3.opExtrude","SWEPT_FACE",FACE,{"disambiguationData":[OSD([sQuery(id+"F2.wireOp",EDGE,"E12.2.0")])]})});
            var Q24;
            Q24=makeQuery(id+"F3.boolean.opBoolean","COPY",FACE,{"derivedFrom":makeQuery(id+"F3.opExtrude","SWEPT_FACE",FACE,{"disambiguationData":[OSD([sQuery(id+"F2.wireOp",EDGE,"E7.1.0")])]})});
            var Q25;
            Q25=makeQuery(id+"F3.boolean.opBoolean","COPY",FACE,{"derivedFrom":makeQuery(id+"F3.opExtrude","SWEPT_FACE",FACE,{"disambiguationData":[OSD([sQuery(id+"F2.wireOp",EDGE,"E7.2.0")])]})});
            var Q26;
            Q26=makeQuery(id+"F3.boolean.opBoolean","COPY",FACE,{"derivedFrom":makeQuery(id+"F3.opExtrude","SWEPT_FACE",FACE,{"disambiguationData":[OSD([sQuery(id+"F2.wireOp",EDGE,"E12.5.0")])]})});
            var Q27;
            Q27=makeQuery(id+"F3.boolean.opBoolean","COPY",FACE,{"derivedFrom":makeQuery(id+"F3.opExtrude","SWEPT_FACE",FACE,{"disambiguationData":[OSD([sQuery(id+"F2.wireOp",EDGE,"E12.4.0")])]})});
            var Q28;
            Q28=makeQuery(id+"F3.boolean.opBoolean","COPY",FACE,{"derivedFrom":makeQuery(id+"F3.opExtrude","SWEPT_FACE",FACE,{"disambiguationData":[OSD([sQuery(id+"F2.wireOp",EDGE,"E12.3.0")])]})});
            var Q29;
            Q29=makeQuery(id+"F3.boolean.opBoolean","COPY",FACE,{"derivedFrom":makeQuery(id+"F3.opExtrude","SWEPT_FACE",FACE,{"disambiguationData":[OSD([sQuery(id+"F2.wireOp",EDGE,"E12.6.0")])]})});
            var Q30;
            Q30=sQuery(id+"F4.wireOp",EDGE,"E21");
            circularPattern(context, id + "F9", {"faces" : qUnion([Q0, Q1, Q2, Q3, Q4, Q5, Q6, Q7, Q8, Q9, Q10, Q11, Q12, Q13, Q14, Q15, Q16, Q17, Q18, Q19, Q20, Q21, Q22, Q23, Q24, Q25, Q26, Q27, Q28, Q29]), "axis" : qUnion([Q30]), "angle" : 70 * degree, "instanceCount" : 2, "oppositeDirection" : true, "patternType" : PatternType.FACE});
        }
        {
            var Q0;
            Q0=makeQuery(id+"F9.opPattern","COPY",FACE,{"derivedFrom":makeQuery(id+"F3.boolean.opBoolean","COPY",FACE,{"derivedFrom":makeQuery(id+"F3.opExtrude","SWEPT_FACE",FACE,{"disambiguationData":[OSD([sQuery(id+"F2.wireOp",EDGE,"E18.13.0")])]})}),"instanceName":"1"});
            var Q1;
            Q1=makeQuery(id+"F9.opPattern","COPY",FACE,{"derivedFrom":makeQuery(id+"F3.boolean.opBoolean","COPY",FACE,{"derivedFrom":makeQuery(id+"F3.opExtrude","SWEPT_FACE",FACE,{"disambiguationData":[OSD([sQuery(id+"F2.wireOp",EDGE,"E18.12.0")])]})}),"instanceName":"1"});
            var Q2;
            Q2=makeQuery(id+"F9.opPattern","COPY",FACE,{"derivedFrom":makeQuery(id+"F3.boolean.opBoolean","COPY",FACE,{"derivedFrom":makeQuery(id+"F3.opExtrude","SWEPT_FACE",FACE,{"disambiguationData":[OSD([sQuery(id+"F2.wireOp",EDGE,"E18.11.0")])]})}),"instanceName":"1"});
            var Q3;
            Q3=makeQuery(id+"F9.opPattern","COPY",FACE,{"derivedFrom":makeQuery(id+"F3.boolean.opBoolean","COPY",FACE,{"derivedFrom":makeQuery(id+"F3.opExtrude","SWEPT_FACE",FACE,{"disambiguationData":[OSD([sQuery(id+"F2.wireOp",EDGE,"E18.10.0")])]})}),"instanceName":"1"});
            var Q4;
            Q4=makeQuery(id+"F9.opPattern","COPY",FACE,{"derivedFrom":makeQuery(id+"F3.boolean.opBoolean","COPY",FACE,{"derivedFrom":makeQuery(id+"F3.opExtrude","SWEPT_FACE",FACE,{"disambiguationData":[OSD([sQuery(id+"F2.wireOp",EDGE,"E18.9.0")])]})}),"instanceName":"1"});
            var Q5;
            Q5=makeQuery(id+"F9.opPattern","COPY",FACE,{"derivedFrom":makeQuery(id+"F3.boolean.opBoolean","COPY",FACE,{"derivedFrom":makeQuery(id+"F3.opExtrude","SWEPT_FACE",FACE,{"disambiguationData":[OSD([sQuery(id+"F2.wireOp",EDGE,"E18.8.0")])]})}),"instanceName":"1"});
            var Q6;
            Q6=makeQuery(id+"F9.opPattern","COPY",FACE,{"derivedFrom":makeQuery(id+"F3.boolean.opBoolean","COPY",FACE,{"derivedFrom":makeQuery(id+"F3.opExtrude","SWEPT_FACE",FACE,{"disambiguationData":[OSD([sQuery(id+"F2.wireOp",EDGE,"E18.7.0")])]})}),"instanceName":"1"});
            var Q7;
            Q7=makeQuery(id+"F9.opPattern","COPY",FACE,{"derivedFrom":makeQuery(id+"F3.boolean.opBoolean","COPY",FACE,{"derivedFrom":makeQuery(id+"F3.opExtrude","SWEPT_FACE",FACE,{"disambiguationData":[OSD([sQuery(id+"F2.wireOp",EDGE,"E18.6.0")])]})}),"instanceName":"1"});
            var Q8;
            Q8=makeQuery(id+"F9.opPattern","COPY",FACE,{"derivedFrom":makeQuery(id+"F3.boolean.opBoolean","COPY",FACE,{"derivedFrom":makeQuery(id+"F3.opExtrude","SWEPT_FACE",FACE,{"disambiguationData":[OSD([sQuery(id+"F2.wireOp",EDGE,"E18.5.0")])]})}),"instanceName":"1"});
            var Q9;
            Q9=makeQuery(id+"F9.opPattern","COPY",FACE,{"derivedFrom":makeQuery(id+"F3.boolean.opBoolean","COPY",FACE,{"derivedFrom":makeQuery(id+"F3.opExtrude","SWEPT_FACE",FACE,{"disambiguationData":[OSD([sQuery(id+"F2.wireOp",EDGE,"E18.4.0")])]})}),"instanceName":"1"});
            var Q10;
            Q10=makeQuery(id+"F9.opPattern","COPY",FACE,{"derivedFrom":makeQuery(id+"F3.boolean.opBoolean","COPY",FACE,{"derivedFrom":makeQuery(id+"F3.opExtrude","SWEPT_FACE",FACE,{"disambiguationData":[OSD([sQuery(id+"F2.wireOp",EDGE,"E18.3.0")])]})}),"instanceName":"1"});
            var Q11;
            Q11=makeQuery(id+"F9.opPattern","COPY",FACE,{"derivedFrom":makeQuery(id+"F3.boolean.opBoolean","COPY",FACE,{"derivedFrom":makeQuery(id+"F3.opExtrude","SWEPT_FACE",FACE,{"disambiguationData":[OSD([sQuery(id+"F2.wireOp",EDGE,"E18.2.0")])]})}),"instanceName":"1"});
            var Q12;
            Q12=makeQuery(id+"F9.opPattern","COPY",FACE,{"derivedFrom":makeQuery(id+"F3.boolean.opBoolean","COPY",FACE,{"derivedFrom":makeQuery(id+"F3.opExtrude","SWEPT_FACE",FACE,{"disambiguationData":[OSD([sQuery(id+"F2.wireOp",EDGE,"E18.1.0")])]})}),"instanceName":"1"});
            var Q13;
            Q13=makeQuery(id+"F9.opPattern","COPY",FACE,{"derivedFrom":makeQuery(id+"F3.boolean.opBoolean","COPY",FACE,{"derivedFrom":makeQuery(id+"F3.opExtrude","SWEPT_FACE",FACE,{"disambiguationData":[OSD([sQuery(id+"F2.wireOp",EDGE,"E17")])]})}),"instanceName":"1"});
            var Q14;
            Q14=makeQuery(id+"F9.opPattern","COPY",FACE,{"derivedFrom":makeQuery(id+"F3.boolean.opBoolean","COPY",FACE,{"derivedFrom":makeQuery(id+"F3.opExtrude","SWEPT_FACE",FACE,{"disambiguationData":[OSD([sQuery(id+"F2.wireOp",EDGE,"E18.14.0")])]})}),"instanceName":"1"});
            var Q15;
            Q15=makeQuery(id+"F9.opPattern","COPY",FACE,{"derivedFrom":makeQuery(id+"F3.boolean.opBoolean","COPY",FACE,{"derivedFrom":makeQuery(id+"F3.opExtrude","SWEPT_FACE",FACE,{"disambiguationData":[OSD([sQuery(id+"F2.wireOp",EDGE,"E11")])]})}),"instanceName":"1"});
            var Q16;
            Q16=makeQuery(id+"F9.opPattern","COPY",FACE,{"derivedFrom":makeQuery(id+"F3.boolean.opBoolean","COPY",FACE,{"derivedFrom":makeQuery(id+"F3.opExtrude","SWEPT_FACE",FACE,{"disambiguationData":[OSD([sQuery(id+"F2.wireOp",EDGE,"E13.1.8.0")])]})}),"instanceName":"1"});
            var Q17;
            Q17=makeQuery(id+"F9.opPattern","COPY",FACE,{"derivedFrom":makeQuery(id+"F3.boolean.opBoolean","COPY",FACE,{"derivedFrom":makeQuery(id+"F3.opExtrude","SWEPT_FACE",FACE,{"disambiguationData":[OSD([sQuery(id+"F2.wireOp",EDGE,"E13.1.7.0")])]})}),"instanceName":"1"});
            var Q18;
            Q18=makeQuery(id+"F9.opPattern","COPY",FACE,{"derivedFrom":makeQuery(id+"F3.boolean.opBoolean","COPY",FACE,{"derivedFrom":makeQuery(id+"F3.opExtrude","SWEPT_FACE",FACE,{"disambiguationData":[OSD([sQuery(id+"F2.wireOp",EDGE,"E12.6.0")])]})}),"instanceName":"1"});
            var Q19;
            Q19=makeQuery(id+"F9.opPattern","COPY",FACE,{"derivedFrom":makeQuery(id+"F3.boolean.opBoolean","COPY",FACE,{"derivedFrom":makeQuery(id+"F3.opExtrude","SWEPT_FACE",FACE,{"disambiguationData":[OSD([sQuery(id+"F2.wireOp",EDGE,"E12.5.0")])]})}),"instanceName":"1"});
            var Q20;
            Q20=makeQuery(id+"F9.opPattern","COPY",FACE,{"derivedFrom":makeQuery(id+"F3.boolean.opBoolean","COPY",FACE,{"derivedFrom":makeQuery(id+"F3.opExtrude","SWEPT_FACE",FACE,{"disambiguationData":[OSD([sQuery(id+"F2.wireOp",EDGE,"E12.4.0")])]})}),"instanceName":"1"});
            var Q21;
            Q21=makeQuery(id+"F9.opPattern","COPY",FACE,{"derivedFrom":makeQuery(id+"F3.boolean.opBoolean","COPY",FACE,{"derivedFrom":makeQuery(id+"F3.opExtrude","SWEPT_FACE",FACE,{"disambiguationData":[OSD([sQuery(id+"F2.wireOp",EDGE,"E12.3.0")])]})}),"instanceName":"1"});
            var Q22;
            Q22=makeQuery(id+"F9.opPattern","COPY",FACE,{"derivedFrom":makeQuery(id+"F3.boolean.opBoolean","COPY",FACE,{"derivedFrom":makeQuery(id+"F3.opExtrude","SWEPT_FACE",FACE,{"disambiguationData":[OSD([sQuery(id+"F2.wireOp",EDGE,"E12.2.0")])]})}),"instanceName":"1"});
            var Q23;
            Q23=makeQuery(id+"F9.opPattern","COPY",FACE,{"derivedFrom":makeQuery(id+"F3.boolean.opBoolean","COPY",FACE,{"derivedFrom":makeQuery(id+"F3.opExtrude","SWEPT_FACE",FACE,{"disambiguationData":[OSD([sQuery(id+"F2.wireOp",EDGE,"E12.1.0")])]})}),"instanceName":"1"});
            var Q24;
            Q24=makeQuery(id+"F9.opPattern","COPY",FACE,{"derivedFrom":makeQuery(id+"F3.boolean.opBoolean","COPY",FACE,{"derivedFrom":makeQuery(id+"F3.opExtrude","SWEPT_FACE",FACE,{"disambiguationData":[OSD([sQuery(id+"F2.wireOp",EDGE,"E6")])]})}),"instanceName":"1"});
            var Q25;
            Q25=makeQuery(id+"F9.opPattern","COPY",FACE,{"derivedFrom":makeQuery(id+"F3.boolean.opBoolean","COPY",FACE,{"derivedFrom":makeQuery(id+"F3.opExtrude","SWEPT_FACE",FACE,{"disambiguationData":[OSD([sQuery(id+"F2.wireOp",EDGE,"E7.4.0")])]})}),"instanceName":"1"});
            var Q26;
            Q26=makeQuery(id+"F9.opPattern","COPY",FACE,{"derivedFrom":makeQuery(id+"F3.boolean.opBoolean","COPY",FACE,{"derivedFrom":makeQuery(id+"F3.opExtrude","SWEPT_FACE",FACE,{"disambiguationData":[OSD([sQuery(id+"F2.wireOp",EDGE,"E7.3.0")])]})}),"instanceName":"1"});
            var Q27;
            Q27=makeQuery(id+"F9.opPattern","COPY",FACE,{"derivedFrom":makeQuery(id+"F3.boolean.opBoolean","COPY",FACE,{"derivedFrom":makeQuery(id+"F3.opExtrude","SWEPT_FACE",FACE,{"disambiguationData":[OSD([sQuery(id+"F2.wireOp",EDGE,"E7.2.0")])]})}),"instanceName":"1"});
            var Q28;
            Q28=makeQuery(id+"F9.opPattern","COPY",FACE,{"derivedFrom":makeQuery(id+"F3.boolean.opBoolean","COPY",FACE,{"derivedFrom":makeQuery(id+"F3.opExtrude","SWEPT_FACE",FACE,{"disambiguationData":[OSD([sQuery(id+"F2.wireOp",EDGE,"E7.1.0")])]})}),"instanceName":"1"});
            var Q29;
            Q29=makeQuery(id+"F9.opPattern","COPY",FACE,{"derivedFrom":makeQuery(id+"F3.boolean.opBoolean","COPY",FACE,{"derivedFrom":makeQuery(id+"F3.opExtrude","SWEPT_FACE",FACE,{"disambiguationData":[OSD([sQuery(id+"F2.wireOp",EDGE,"E5")])]})}),"instanceName":"1"});
            var Q30;
            Q30=sQuery(id+"F0.wireOp",EDGE,"E2");
            circularPattern(context, id + "F10", {"faces" : qUnion([Q0, Q1, Q2, Q3, Q4, Q5, Q6, Q7, Q8, Q9, Q10, Q11, Q12, Q13, Q14, Q15, Q16, Q17, Q18, Q19, Q20, Q21, Q22, Q23, Q24, Q25, Q26, Q27, Q28, Q29]), "axis" : qUnion([Q30]), "angle" : 360 * degree, "instanceCount" : round(13), "equalSpace" : true, "patternType" : PatternType.FACE});
        }
    });
